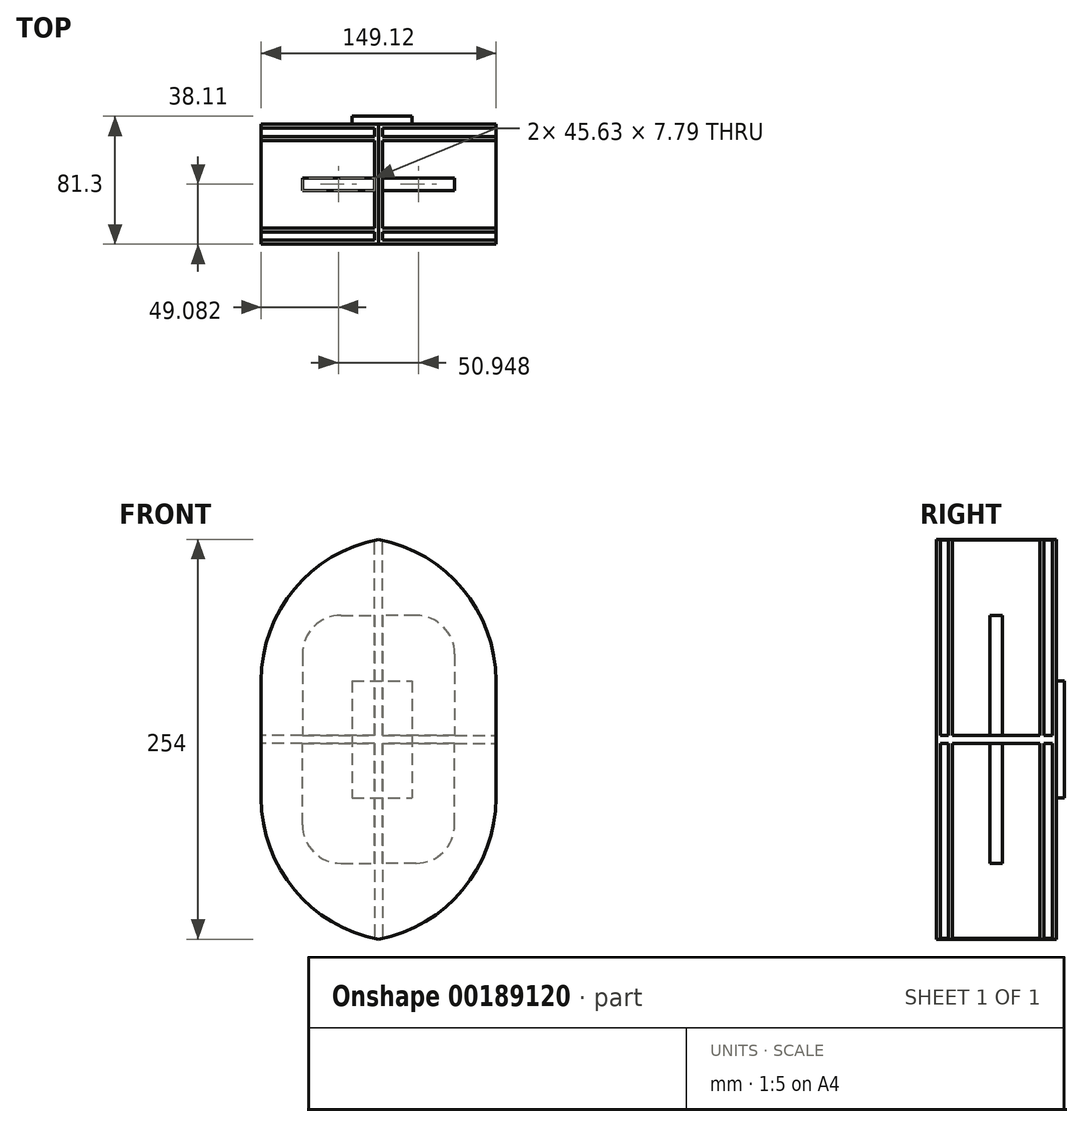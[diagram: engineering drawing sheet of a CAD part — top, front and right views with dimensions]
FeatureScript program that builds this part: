
annotation { "Feature Type Name" : "Feature", "Feature Type Description" : "" }
export const myFeature = defineFeature(function(context is Context, id is Id, definition is map)
    precondition{}
    {
        {
            var Q0;
            Q0=qCreatedBy(makeId("Top.planeOp"),FACE);
            var sketch = newSketch(context, id + "F0", { "sketchPlane" : qUnion([Q0])});
            skLineSegment(sketch, "E0.bottom", {"start": v(-35.05, -30.32) * mm, "end": v(39.5, -30.32) * mm});
            skLineSegment(sketch, "E0.top", {"start": v(-35.05, 38.11) * mm, "end": v(39.5, 38.11) * mm});
            skLineSegment(sketch, "E0.left", {"start": v(-35.05, -30.32) * mm, "end": v(-35.05, 38.11) * mm});
            skLineSegment(sketch, "E0.right", {"start": v(39.5, -30.32) * mm, "end": v(39.5, 38.11) * mm});
            skSolve(sketch);
        }
        {
            var Q0;
            Q0=makeQuery(id+"F0.imprint","IMPRINT",FACE,{"disambiguationData":[TD([[makeQuery(id+"F0.imprint","IMPRINT",EDGE,{"derivedFrom":sQuery(id+"F0.wireOp",EDGE,"E0.bottom")}),1.0]])]});
            extrude(context, id + "F1", {"entities" : qUnion([Q0]), "depth" : 127 * mm});
        }
        {
            var Q0;
            Q0=makeQuery(id+"F1.opExtrude","CAP_FACE",FACE,{"disambiguationData":[OSD([sQuery(id+"F0.wireOp",EDGE,"E0.bottom"),sQuery(id+"F0.wireOp",EDGE,"E0.top"),sQuery(id+"F0.wireOp",EDGE,"E0.left"),sQuery(id+"F0.wireOp",EDGE,"E0.right")])],"isStart":false});
            var Q1;
            Q1=makeQuery(id+"F1.opExtrude","SWEPT_FACE",FACE,{"disambiguationData":[OSD([sQuery(id+"F0.wireOp",EDGE,"E0.right")])]});
            shell(context, id + "F2", {"entities" : qUnion([Q0, Q1]), "thickness" : 2.54 * mm});
        }
        {
            var Q0;
            Q0=makeQuery(id+"F1.opExtrude","CAP_EDGE",EDGE,{"disambiguationData":[OSD([sQuery(id+"F0.wireOp",EDGE,"E0.right")])],"isStart":false});
            fillet(context, id + "F3", {"entities" : qUnion([Q0]), "radius" : 91.37 * mm, "tangentPropagation" : true, "allowEdgeOverflow" : false});
        }
        {
            var Q0;
            Q0=makeQuery(id+"F1.opExtrude","SWEPT_BODY",BODY,{"disambiguationData":[OSD([sQuery(id+"F0.wireOp",EDGE,"E0.bottom"),sQuery(id+"F0.wireOp",EDGE,"E0.top"),sQuery(id+"F0.wireOp",EDGE,"E0.left"),sQuery(id+"F0.wireOp",EDGE,"E0.right")])]});
            var Q1;
            Q1=qCreatedBy(makeId("Front.planeOp"),FACE);
            mirror(context, id + "F4", {"operationType" : NewBodyOperationType.ADD, "entities" : qUnion([Q0]), "mirrorPlane" : qUnion([Q1])});
        }
        {
            var Q0;
            Q0=makeQuery(id+"F1.opExtrude","SWEPT_BODY",BODY,{"disambiguationData":[OSD([sQuery(id+"F0.wireOp",EDGE,"E0.bottom"),sQuery(id+"F0.wireOp",EDGE,"E0.top"),sQuery(id+"F0.wireOp",EDGE,"E0.left"),sQuery(id+"F0.wireOp",EDGE,"E0.right")])]});
            var Q1;
            Q1=qCreatedBy(makeId("Top.planeOp"),FACE);
            mirror(context, id + "F5", {"operationType" : NewBodyOperationType.ADD, "entities" : qUnion([Q0]), "mirrorPlane" : qUnion([Q1])});
        }
        {
            var Q0;
            {var subQ0=sQuery(id+"F0.wireOp",EDGE,"E0.left");var subQ1=sQuery(id+"F0.wireOp",EDGE,"E0.bottom");var subQ2=makeQuery(id+"F2.opShell","OFFSET_FACE",FACE,{"disambiguationData":[OSD([subQ1])]});var subQ3=sQuery(id+"F0.wireOp",EDGE,"E0.right");Q0=makeQuery(id+"F5.opPattern","COPY",FACE,{"derivedFrom":makeQuery(id+"F4.boolean.opBoolean","SPLIT",FACE,{"disambiguationData":[TD([subQ2])],"derivedFrom":makeQuery(id+"F2.opShell","OFFSET_FACE",FACE,{"disambiguationData":[OSD([subQ1,sQuery(id+"F0.wireOp",EDGE,"E0.top"),subQ0,subQ3])]})}),"instanceName":"1"});}
            var sketch = newSketch(context, id + "F6", { "sketchPlane" : qUnion([Q0])});
            skLineSegment(sketch, "E1.bottom", {"start": v(13.23, -3.9) * mm, "end": v(-32.4, -3.9) * mm});
            skLineSegment(sketch, "E1.top", {"start": v(13.23, 3.9) * mm, "end": v(-32.4, 3.9) * mm});
            skLineSegment(sketch, "E1.left", {"start": v(13.23, -3.9) * mm, "end": v(13.23, 3.9) * mm});
            skLineSegment(sketch, "E1.right", {"start": v(-32.4, -3.9) * mm, "end": v(-32.4, 3.9) * mm});
            skPoint(sketch, "E1.middle", {"position": v(-9.58, 0) * mm});
            skSolve(sketch);
        }
        {
            var Q0;
            Q0=makeQuery(id+"F6.imprint","IMPRINT",FACE,{"disambiguationData":[TD([[makeQuery(id+"F6.imprint","IMPRINT",EDGE,{"derivedFrom":sQuery(id+"F6.wireOp",EDGE,"E1.bottom")}),-1.0]])]});
            extrude(context, id + "F7", {"entities" : qUnion([Q0]), "operationType" : NewBodyOperationType.ADD, "depth" : 76.2 * mm});
        }
        {
            var Q0;
            Q0=makeQuery(id+"F7.opExtrude","CAP_EDGE",EDGE,{"disambiguationData":[OSD([sQuery(id+"F6.wireOp",EDGE,"E1.left")])],"isStart":false});
            fillet(context, id + "F8", {"entities" : qUnion([Q0]), "radius" : 24.53 * mm, "tangentPropagation" : true, "allowEdgeOverflow" : false});
        }
        {
            var Q0;
            Q0=makeQuery(id+"F1.opExtrude","SWEPT_BODY",BODY,{"disambiguationData":[OSD([sQuery(id+"F0.wireOp",EDGE,"E0.bottom"),sQuery(id+"F0.wireOp",EDGE,"E0.top"),sQuery(id+"F0.wireOp",EDGE,"E0.left"),sQuery(id+"F0.wireOp",EDGE,"E0.right")])]});
            var Q1;
            Q1=qCreatedBy(makeId("Top.planeOp"),FACE);
            mirror(context, id + "F9", {"operationType" : NewBodyOperationType.ADD, "entities" : qUnion([Q0]), "mirrorPlane" : qUnion([Q1])});
        }
        {
            var Q0;
            Q0=makeQuery(id+"F1.opExtrude","SWEPT_BODY",BODY,{"disambiguationData":[OSD([sQuery(id+"F0.wireOp",EDGE,"E0.bottom"),sQuery(id+"F0.wireOp",EDGE,"E0.top"),sQuery(id+"F0.wireOp",EDGE,"E0.left"),sQuery(id+"F0.wireOp",EDGE,"E0.right")])]});
            var Q1;
            {var subQ0=makeQuery(id+"F1.opExtrude","SWEPT_FACE",FACE,{"disambiguationData":[OSD([sQuery(id+"F0.wireOp",EDGE,"E0.left")])]});var subQ1=makeQuery(id+"F4.boolean.opBoolean","MERGE",FACE,{"derivedFrom":[subQ0,makeQuery(id+"F4.opPattern","COPY",FACE,{"derivedFrom":subQ0,"instanceName":"1"})]});Q1=makeQuery(id+"F5.boolean.opBoolean","MERGE",FACE,{"derivedFrom":[subQ1,makeQuery(id+"F5.opPattern","COPY",FACE,{"derivedFrom":subQ1,"instanceName":"1"})]});}
            mirror(context, id + "F10", {"operationType" : NewBodyOperationType.ADD, "entities" : qUnion([Q0]), "mirrorPlane" : qUnion([Q1])});
        }
        {
            var Q0;
            {var subQ0=makeQuery(id+"F1.opExtrude","SWEPT_FACE",FACE,{"disambiguationData":[OSD([sQuery(id+"F0.wireOp",EDGE,"E0.top")])]});var subQ1=makeQuery(id+"F5.boolean.opBoolean","MERGE",FACE,{"derivedFrom":[subQ0,makeQuery(id+"F5.opPattern","COPY",FACE,{"derivedFrom":subQ0,"instanceName":"1"})]});Q0=makeQuery(id+"F10.boolean.opBoolean","MERGE",FACE,{"derivedFrom":[subQ1,makeQuery(id+"F10.opPattern","COPY",FACE,{"derivedFrom":subQ1,"instanceName":"1"})]});}
            var sketch = newSketch(context, id + "F11", { "sketchPlane" : qUnion([Q0])});
            skLineSegment(sketch, "E2.bottom", {"start": v(51.86, 37.2) * mm, "end": v(13.83, 37.2) * mm});
            skLineSegment(sketch, "E2.top", {"start": v(51.86, -37.2) * mm, "end": v(13.83, -37.2) * mm});
            skLineSegment(sketch, "E2.left", {"start": v(51.86, 37.2) * mm, "end": v(51.86, -37.2) * mm});
            skLineSegment(sketch, "E2.right", {"start": v(13.83, 37.2) * mm, "end": v(13.83, -37.2) * mm});
            skPoint(sketch, "E2.middle", {"position": v(32.85, 0) * mm});
            skSolve(sketch);
        }
        {
            var Q0;
            Q0 = qSketchRegion(id + "F11", true);
            extrude(context, id + "F12", {"entities" : qUnion([Q0]), "operationType" : NewBodyOperationType.ADD, "depth" : 5.08 * mm});
        }
        {
            var Q0;
            {var subQ0=makeQuery(id+"F4.opPattern","COPY",FACE,{"derivedFrom":makeQuery(id+"F1.opExtrude","SWEPT_FACE",FACE,{"disambiguationData":[OSD([sQuery(id+"F0.wireOp",EDGE,"E0.top")])]}),"instanceName":"1"});var subQ1=makeQuery(id+"F5.boolean.opBoolean","MERGE",FACE,{"derivedFrom":[subQ0,makeQuery(id+"F5.opPattern","COPY",FACE,{"derivedFrom":subQ0,"instanceName":"1"})]});Q0=makeQuery(id+"F10.boolean.opBoolean","MERGE",FACE,{"derivedFrom":[subQ1,makeQuery(id+"F10.opPattern","COPY",FACE,{"derivedFrom":subQ1,"instanceName":"1"})]});}
            var sketch = newSketch(context, id + "F13", { "sketchPlane" : qUnion([Q0])});
            skLineSegment(sketch, "E3.bottom", {"start": v(-92.59, -90.3) * mm, "end": v(22.12, -90.3) * mm});
            skLineSegment(sketch, "E3.top", {"start": v(-92.59, 90.8) * mm, "end": v(22.12, 90.8) * mm});
            skLineSegment(sketch, "E3.left", {"start": v(-92.59, -90.3) * mm, "end": v(-92.59, 90.8) * mm});
            skLineSegment(sketch, "E3.right", {"start": v(22.12, -90.3) * mm, "end": v(22.12, 90.8) * mm});
            skSolve(sketch);
        }
        {
            var Q0;
            Q0=sQuery(id+"F13.wireOp",EDGE,"E3.bottom");
            var Q1;
            Q1=sQuery(id+"F13.wireOp",EDGE,"E3.right");
            var Q2;
            Q2=sQuery(id+"F13.wireOp",EDGE,"E3.top");
            var Q3;
            Q3=sQuery(id+"F13.wireOp",EDGE,"E3.left");
            extrude(context, id + "F14", {"bodyType" : ToolBodyType.SURFACE, "surfaceEntities" : qUnion([Q0, Q1, Q2, Q3]), "depth" : 10.16 * mm});
        }
    });
